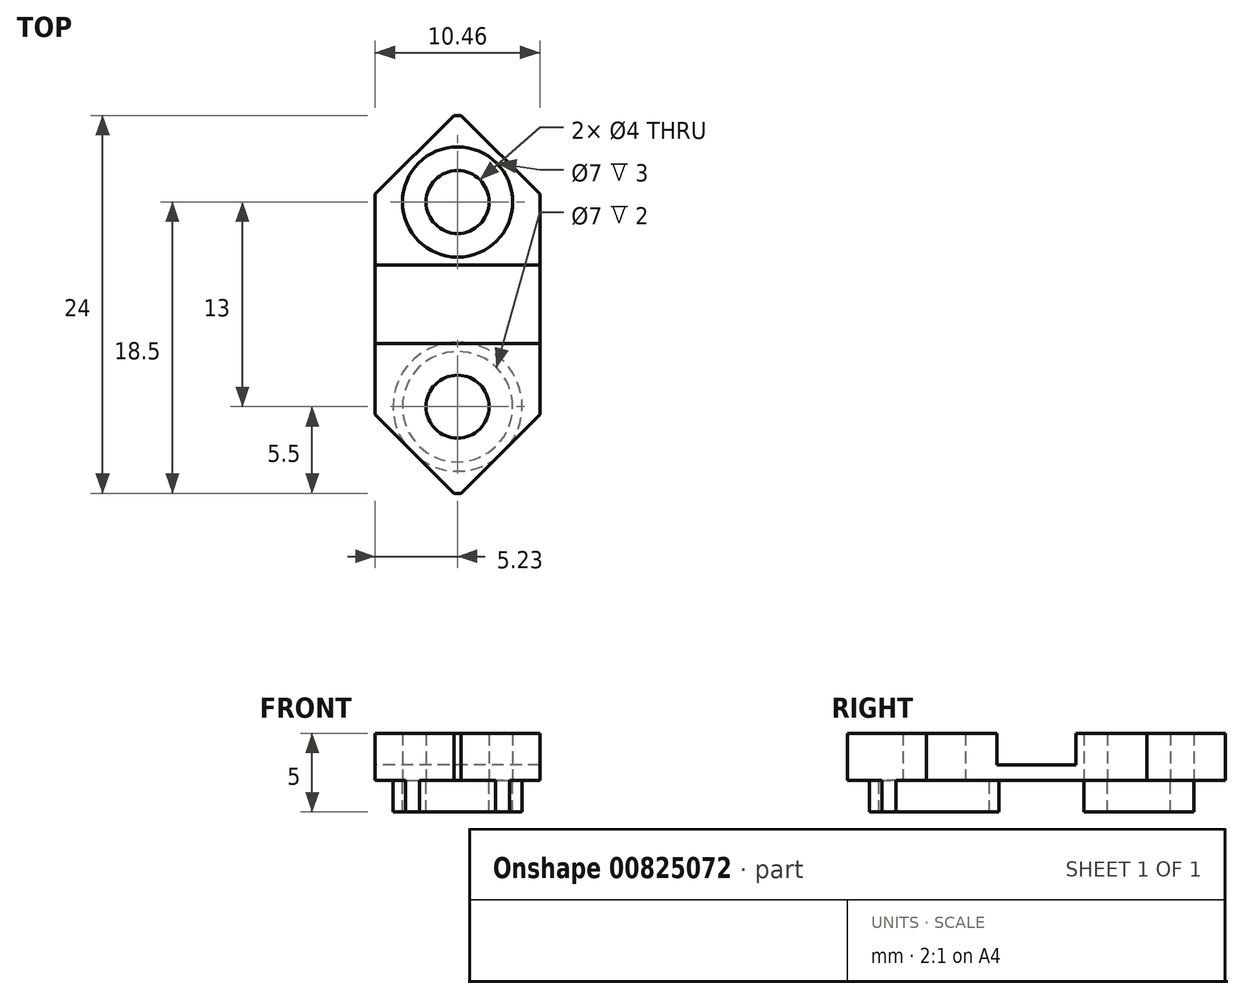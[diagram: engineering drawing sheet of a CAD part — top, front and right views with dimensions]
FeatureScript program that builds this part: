
annotation { "Feature Type Name" : "Feature", "Feature Type Description" : "" }
export const myFeature = defineFeature(function(context is Context, id is Id, definition is map)
    precondition{}
    {
        {
            var Q0;
            Q0=qCreatedBy(makeId("Top.planeOp"),FACE);
            var sketch = newSketch(context, id + "F0", { "sketchPlane" : qUnion([Q0])});
            skLineSegment(sketch, "E0.bottom", {"start": v(-5, 2.5) * mm, "end": v(5, 2.5) * mm});
            skLineSegment(sketch, "E0.top", {"start": v(-5, -2.5) * mm, "end": v(5, -2.5) * mm});
            skLineSegment(sketch, "E0.left", {"start": v(-5, 2.5) * mm, "end": v(-5, -2.5) * mm});
            skLineSegment(sketch, "E0.right", {"start": v(5, 2.5) * mm, "end": v(5, -2.5) * mm});
            skPoint(sketch, "E0.middle", {"position": v(0, 0) * mm});
            skLineSegment(sketch, "E1.bottom", {"start": v(-5.23, 12) * mm, "end": v(5.23, 12) * mm});
            skLineSegment(sketch, "E1.top", {"start": v(-5.23, -12) * mm, "end": v(5.23, -12) * mm});
            skLineSegment(sketch, "E1.left", {"start": v(-5.23, 12) * mm, "end": v(-5.23, -12) * mm});
            skLineSegment(sketch, "E1.right", {"start": v(5.23, 12) * mm, "end": v(5.23, -12) * mm});
            skSolve(sketch);
        }
        {
            var Q0;
            Q0=makeQuery(id+"F0.imprint","IMPRINT",FACE,{"disambiguationData":[TD([[makeQuery(id+"F0.imprint","IMPRINT",EDGE,{"derivedFrom":sQuery(id+"F0.wireOp",EDGE,"E0.bottom")}),1.0]])]});
            var Q1;
            Q1=makeQuery(id+"F0.imprint","IMPRINT",FACE,{"disambiguationData":[TD([[makeQuery(id+"F0.imprint","IMPRINT",EDGE,{"derivedFrom":sQuery(id+"F0.wireOp",EDGE,"E0.bottom")}),-1.0]])]});
            extrude(context, id + "F1", {"entities" : qUnion([Q0, Q1]), "depth" : 1 * mm, "offsetDistance" : 25 * mm});
        }
        {
            var Q0;
            Q0=makeQuery(id+"F0.imprint","IMPRINT",FACE,{"disambiguationData":[TD([[makeQuery(id+"F0.imprint","IMPRINT",EDGE,{"derivedFrom":sQuery(id+"F0.wireOp",EDGE,"E0.bottom")}),1.0]])]});
            extrude(context, id + "F2", {"entities" : qUnion([Q0]), "operationType" : NewBodyOperationType.ADD, "depth" : 3 * mm, "offsetDistance" : 25 * mm});
        }
        {
            var Q0;
            Q0=makeQuery(id+"F2.opExtrude","SWEPT_FACE",FACE,{"disambiguationData":[OSD([sQuery(id+"F0.wireOp",EDGE,"E0.left")])]});
            extrude(context, id + "F3", {"entities" : qUnion([Q0]), "operationType" : NewBodyOperationType.REMOVE, "oppositeDirection" : true, "depth" : 25 * mm, "offsetDistance" : 25 * mm});
        }
        {
            var Q0;
            Q0=makeQuery(id+"F2.opExtrude","SWEPT_FACE",FACE,{"disambiguationData":[OSD([sQuery(id+"F0.wireOp",EDGE,"E0.right")])]});
            extrude(context, id + "F4", {"entities" : qUnion([Q0]), "operationType" : NewBodyOperationType.REMOVE, "oppositeDirection" : true, "depth" : 25 * mm, "offsetDistance" : 25 * mm});
        }
        {
            var Q0;
            {var subQ0=sQuery(id+"F0.wireOp",EDGE,"E1.left");var subQ1=sQuery(id+"F0.wireOp",EDGE,"E1.top");Q0=makeQuery(id+"F2.boolean.opBoolean","MERGE",EDGE,{"derivedFrom":[makeQuery(id+"F1.opExtrude","SWEPT_EDGE",EDGE,{"disambiguationData":[OSD([subQ1,subQ0])]}),makeQuery(id+"F2.opExtrude","SWEPT_EDGE",EDGE,{"disambiguationData":[OSD([subQ1,subQ0])]})]});}
            var Q1;
            {var subQ0=sQuery(id+"F0.wireOp",EDGE,"E1.right");var subQ1=sQuery(id+"F0.wireOp",EDGE,"E1.top");Q1=makeQuery(id+"F2.boolean.opBoolean","MERGE",EDGE,{"derivedFrom":[makeQuery(id+"F1.opExtrude","SWEPT_EDGE",EDGE,{"disambiguationData":[OSD([subQ1,subQ0])]}),makeQuery(id+"F2.opExtrude","SWEPT_EDGE",EDGE,{"disambiguationData":[OSD([subQ1,subQ0])]})]});}
            var Q2;
            {var subQ0=sQuery(id+"F0.wireOp",EDGE,"E1.right");var subQ1=sQuery(id+"F0.wireOp",EDGE,"E1.bottom");Q2=makeQuery(id+"F2.boolean.opBoolean","MERGE",EDGE,{"derivedFrom":[makeQuery(id+"F1.opExtrude","SWEPT_EDGE",EDGE,{"disambiguationData":[OSD([subQ1,subQ0])]}),makeQuery(id+"F2.opExtrude","SWEPT_EDGE",EDGE,{"disambiguationData":[OSD([subQ1,subQ0])]})]});}
            var Q3;
            {var subQ0=sQuery(id+"F0.wireOp",EDGE,"E1.left");var subQ1=sQuery(id+"F0.wireOp",EDGE,"E1.bottom");Q3=makeQuery(id+"F2.boolean.opBoolean","MERGE",EDGE,{"derivedFrom":[makeQuery(id+"F1.opExtrude","SWEPT_EDGE",EDGE,{"disambiguationData":[OSD([subQ1,subQ0])]}),makeQuery(id+"F2.opExtrude","SWEPT_EDGE",EDGE,{"disambiguationData":[OSD([subQ1,subQ0])]})]});}
            chamfer(context, id + "F5", {"entities" : qUnion([Q0, Q1, Q2, Q3]), "width" : 5 * mm, "tangentPropagation" : true});
        }
        {
            var Q0;
            Q0=makeQuery(id+"F1.opExtrude","CAP_FACE",FACE,{"disambiguationData":[OSD([sQuery(id+"F0.wireOp",EDGE,"E1.bottom"),sQuery(id+"F0.wireOp",EDGE,"E1.top"),sQuery(id+"F0.wireOp",EDGE,"E1.left"),sQuery(id+"F0.wireOp",EDGE,"E1.right")])],"isStart":true});
            var sketch = newSketch(context, id + "F6", { "sketchPlane" : qUnion([Q0])});
            skLineSegment(sketch, "E2", {"start": v(0, 12) * mm, "end": v(0, 6.5) * mm});
            skCircle(sketch, "E3", {"center": v(0, 6.5) * mm, "radius": 4.1 * mm});
            skCircle(sketch, "E4", {"center": v(0, 6.5) * mm, "radius": 2 * mm});
            skCircle(sketch, "E5.MirrorC", {"center": v(0, -6.5) * mm, "radius": 2 * mm});
            skCircle(sketch, "E6", {"center": v(0, 6.5) * mm, "radius": 3.5 * mm});
            skCircle(sketch, "E7.MirrorC", {"center": v(0, -6.5) * mm, "radius": 3.5 * mm});
            skCircle(sketch, "E8.MirrorC", {"center": v(0, -6.5) * mm, "radius": 4.1 * mm});
            skSolve(sketch);
        }
        {
            var Q0;
            Q0=makeQuery(id+"F6.imprint","IMPRINT",FACE,{"disambiguationData":[TD([[makeQuery(id+"F6.imprint","IMPRINT",EDGE,{"derivedFrom":sQuery(id+"F6.wireOp",EDGE,"E4")}),1.0]])]});
            var Q1;
            Q1=makeQuery(id+"F6.imprint","IMPRINT",FACE,{"disambiguationData":[TD([[makeQuery(id+"F6.imprint","IMPRINT",EDGE,{"derivedFrom":sQuery(id+"F6.wireOp",EDGE,"E5.MirrorC")}),-1.0]])]});
            extrude(context, id + "F7", {"entities" : qUnion([Q0, Q1]), "operationType" : NewBodyOperationType.REMOVE, "oppositeDirection" : true, "depth" : 25 * mm, "offsetDistance" : 25 * mm});
        }
        {
            var Q0;
            Q0=makeQuery(id+"F6.imprint","IMPRINT",FACE,{"disambiguationData":[TD([[makeQuery(id+"F6.imprint","IMPRINT",EDGE,{"derivedFrom":sQuery(id+"F6.wireOp",EDGE,"E3")}),1.0]])]});
            var Q1;
            Q1=makeQuery(id+"F6.imprint","IMPRINT",FACE,{"disambiguationData":[TD([[makeQuery(id+"F6.imprint","IMPRINT",EDGE,{"derivedFrom":sQuery(id+"F6.wireOp",EDGE,"E7.MirrorC")}),1.0]])]});
            extrude(context, id + "F8", {"entities" : qUnion([Q0, Q1]), "operationType" : NewBodyOperationType.ADD, "depth" : 2 * mm, "offsetDistance" : 25 * mm});
        }
    });
